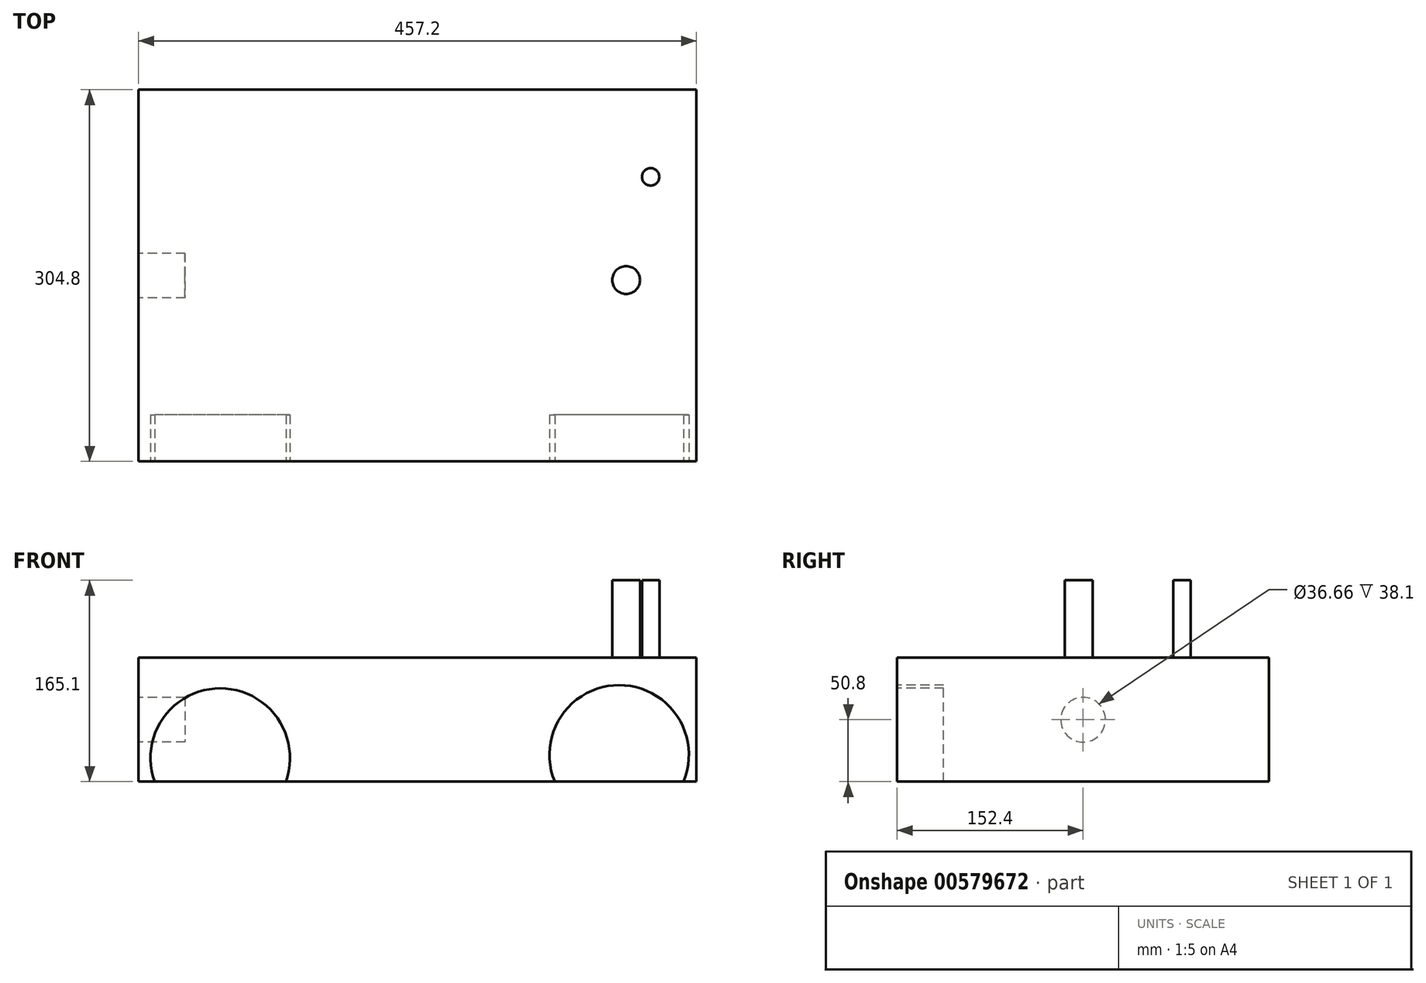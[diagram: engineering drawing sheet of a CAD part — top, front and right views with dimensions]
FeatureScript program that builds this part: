
annotation { "Feature Type Name" : "Feature", "Feature Type Description" : "" }
export const myFeature = defineFeature(function(context is Context, id is Id, definition is map)
    precondition{}
    {
        {
            var Q0;
            Q0=qCreatedBy(makeId("Front.planeOp"),FACE);
            var sketch = newSketch(context, id + "F0", { "sketchPlane" : qUnion([Q0])});
            skLineSegment(sketch, "E0.bottom", {"start": v(228.6, -50.8) * mm, "end": v(-228.6, -50.8) * mm});
            skLineSegment(sketch, "E0.top", {"start": v(228.6, 50.8) * mm, "end": v(-228.6, 50.8) * mm});
            skLineSegment(sketch, "E0.left", {"start": v(228.6, -50.8) * mm, "end": v(228.6, 50.8) * mm});
            skLineSegment(sketch, "E0.right", {"start": v(-228.6, -50.8) * mm, "end": v(-228.6, 50.8) * mm});
            skPoint(sketch, "E0.middle", {"position": v(0, 0) * mm});
            skSolve(sketch);
        }
        {
            var Q0;
            Q0 = qSketchRegion(id + "F0", true);
            extrude(context, id + "F1", {"entities" : qUnion([Q0]), "depth" : 304.8 * mm, "offsetDistance" : 25.4 * mm});
        }
        {
            var Q0;
            Q0=makeQuery(id+"F1.opExtrude","CAP_FACE",FACE,{"disambiguationData":[OSD([sQuery(id+"F0.wireOp",EDGE,"E0.bottom"),sQuery(id+"F0.wireOp",EDGE,"E0.top"),sQuery(id+"F0.wireOp",EDGE,"E0.left"),sQuery(id+"F0.wireOp",EDGE,"E0.right")])],"isStart":false});
            var sketch = newSketch(context, id + "F2", { "sketchPlane" : qUnion([Q0])});
            skCircle(sketch, "E1", {"center": v(-161.7, -31.46) * mm, "radius": 57.15 * mm});
            skCircle(sketch, "E2", {"center": v(165.22, -28.77) * mm, "radius": 57.15 * mm});
            skSolve(sketch);
        }
        {
            var Q0;
            Q0 = qSketchRegion(id + "F2", true);
            extrude(context, id + "F3", {"entities" : qUnion([Q0]), "operationType" : NewBodyOperationType.REMOVE, "oppositeDirection" : true, "depth" : 38.1 * mm, "offsetDistance" : 25.4 * mm});
        }
        {
            var Q0;
            Q0=makeQuery(id+"F1.opExtrude","SWEPT_FACE",FACE,{"disambiguationData":[OSD([sQuery(id+"F0.wireOp",EDGE,"E0.top")])]});
            var sketch = newSketch(context, id + "F4", { "sketchPlane" : qUnion([Q0])});
            skCircle(sketch, "E3", {"center": v(191, -71.44) * mm, "radius": 7.13 * mm});
            skCircle(sketch, "E4", {"center": v(170.92, -156.07) * mm, "radius": 11.4 * mm});
            skSolve(sketch);
        }
        {
            var Q0;
            Q0 = qSketchRegion(id + "F4", true);
            extrude(context, id + "F5", {"entities" : qUnion([Q0]), "operationType" : NewBodyOperationType.ADD, "depth" : 63.5 * mm, "offsetDistance" : 25.4 * mm});
        }
        {
            var Q0;
            Q0 = qSketchRegion(id + "F4", true);
            extrude(context, id + "F6", {"entities" : qUnion([Q0]), "operationType" : NewBodyOperationType.ADD, "depth" : 63.5 * mm, "offsetDistance" : 25.4 * mm});
        }
        {
            var Q0;
            Q0=makeQuery(id+"F1.opExtrude","SWEPT_FACE",FACE,{"disambiguationData":[OSD([sQuery(id+"F0.wireOp",EDGE,"E0.right")])]});
            var sketch = newSketch(context, id + "F7", { "sketchPlane" : qUnion([Q0])});
            skCircle(sketch, "E5", {"center": v(152.4, 0) * mm, "radius": 18.33 * mm});
            skSolve(sketch);
        }
        {
            var Q0;
            Q0 = qSketchRegion(id + "F7", true);
            extrude(context, id + "F8", {"entities" : qUnion([Q0]), "operationType" : NewBodyOperationType.REMOVE, "oppositeDirection" : true, "depth" : 38.1 * mm, "offsetDistance" : 25.4 * mm});
        }
    });
